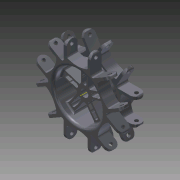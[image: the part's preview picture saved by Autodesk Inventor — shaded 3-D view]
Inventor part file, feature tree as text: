
AUTODESK INVENTOR PART (.ipt)
format: ipt  version: 2011 (Build 150239000, 239)  size: 891,392 bytes
history: native  units: in
note: dims shown in document units (in); Inventor stores cm internally (conversion verified against a paired STEP export)
features: extrude x18, sketch x18, pattern_circular x11, fillet x10, other x1, plane x1
ambient origin geometry x8: Origin, YZ Plane, XZ Plane, XY Plane, X Axis, Y Axis, Z Axis, Center Point
bodies: Solid1 (feature_tree)
feature tree (59):
  extrude  "Extrusion1"  Depth=0.75in TaperAngle=0.0deg
  extrude  "Extrusion2"  Depth=0.7156in
  other  "Work Axis1"
  pattern_circular  "Circular Pattern1"  Count=6 Angle=360.0deg
  extrude  "Extrusion3"  Depth=0.1875in
  pattern_circular  "Circular Pattern2"  Count=6 Angle=360.0deg
  fillet  "Fillet1"  Radius=0.125in
  extrude  "Extrusion4"  Depth=0.75in TaperAngle=0.0deg
  extrude  "Extrusion5"  Depth=0.25in TaperAngle=0.0deg
  extrude  "Extrusion6"  Depth=0.75in TaperAngle=0.0deg
  extrude  "Extrusion7"  Depth=0.7156in
  pattern_circular  "Circular Pattern3"  Count=6 Angle=360.0deg
  extrude  "Extrusion8"  Depth=0.1875in
  extrude  "Extrusion9"  Depth=0.75in TaperAngle=0.0deg
  pattern_circular  "Circular Pattern4"  Count=6 Angle=360.0deg
  plane  "Work Plane1"
  fillet  "Fillet2"  [1 undecoded]
  fillet  "Fillet3"  Radius=0.7156in
  fillet  "Fillet4"  Radius=0.7156in
  fillet  "Fillet8"  Radius=0.501in
  fillet  "Fillet9"  Radius=1.0in
  extrude  "Extrusion11"  Depth=0.25in
  pattern_circular  "Circular Pattern6"  [2 undecoded]
  extrude  "Extrusion12"  Depth=1.9685in TaperAngle=360.0deg
  pattern_circular  "Circular Pattern7"  [2 undecoded]
  extrude  "Extrusion10"  Depth=0.125in
  pattern_circular  "Circular Pattern5"  [2 undecoded]
  fillet  "Fillet16"  Radius=0.125in
  extrude  "Extrusion15"  Depth=0.125in
  fillet  "Fillet17"  Radius=0.25in
  pattern_circular  "Circular Pattern9"  [2 undecoded]
  extrude  "Extrusion16"  Depth=0.75in TaperAngle=0.0deg
  extrude  "Extrusion17"  Depth=2.3622in TaperAngle=360.0deg
  pattern_circular  "Circular Pattern10"  [2 undecoded]
  extrude  "Extrusion18"  Depth=0.25in
  extrude  "Extrusion19"  Depth=0.75in TaperAngle=0.0deg
  pattern_circular  "Circular Pattern11"  Count=6 Angle=360.0deg
  fillet  "Fillet18"  Radius=4378.1713in
  fillet  "Fillet21"  Radius=4378.1713in
  extrude  "Extrusion21"  Depth=0.125in
  pattern_circular  "Circular Pattern12"  [2 undecoded]
  sketch  "Sketch1"  dims[d0=6.0in d1=0.75in d2=0.0in]
  sketch  "Sketch2"  dims[d5=1.7in d6=0.7156in]
  sketch  "Sketch3"  dims[d7=0.7156in]
  sketch  "Sketch4"  dims[d8=2.0in]
  sketch  "Sketch5"  dims[d9=2.0in]
  sketch  "Sketch6"  dims[d10=0.75in d11=0.0in d12=2.3622in d13=360.0deg]
  sketch  "Sketch7"  dims[d15=0.1875in d16=0.1875in]
  sketch  "Sketch8"  dims[d17=0.75in d18=0.0in d19=2.3622in d20=360.0deg d22=0.125in]
  sketch  "Sketch9"  dims[d23=3.2in d24=0.75in d25=0.0in]
  sketch  "Sketch10"  dims[d26=3.45in d27=0.25in d28=0.0in]
  sketch  "Sketch11"  dims[d29=6.0in d30=0.75in d31=0.0in]
  sketch  "Sketch12"  dims[d32=0.7156in d33=0.7156in]
  sketch  "Sketch16"  dims[d34=2.0in]
  sketch  "Sketch17"  dims[d35=1.7in]
  sketch  "Sketch18"  dims[d36=0.75in d37=0.0in d38=2.3622in d39=360.0deg]
  sketch  "Sketch19"  dims[d41=0.75in d42=0.0in d43=0.1875in]
  sketch  "Sketch20"  dims[d44=0.1875in d45=0.75in d46=0.0in d47=2.3622in d48=360.0deg d50=-0.875in d51=0.7156in d52=0.7156in d53=0.501in d54=1.0in]
  sketch  "Sketch22"  dims[d55=0.25in d56=0.25in d57=0.75in d58=0.0in d59=1.9685in d60=360.0deg d62=0.125in d63=0.125in d64=0.125in d68=0.125in d69=0.125in d70=0.25in d71=0.25in d72=0.75in d73=0.0in d74=2.3622in d75=360.0deg d77=0.25in d78=0.25in d79=0.75in d80=0.0in d81=2.3622in d82=360.0deg d85=4378.1713in d86=4378.1713in d110=0.125in d111=0.125in d112=0.125in d116=1.0in d117=0.0in d118=0.125in d122=0.95in d123=1.9685in d124=360.0deg d126=0.375in d127=1.0in d128=0.0in d129=0.375in d130=1.0in d131=0.0in d132=2.3622in d133=360.0deg d135=0.375in d136=1.0in d137=0.0in d138=0.375in d139=1.0in d140=0.0in d141=2.3622in d142=360.0deg d146=3.2in d147=1.169in d148=0.465in d149=0.125in d154=0.1875in d155=0.94in d156=0.3in d157=1.0in d158=0.0in d159=1.9685in d160=360.0deg]
note: 13 required parameter values undecoded (feature->parameter linkage not recoverable at this tier; creation-order binding heuristic only, values carry confidence <= 0.55)
